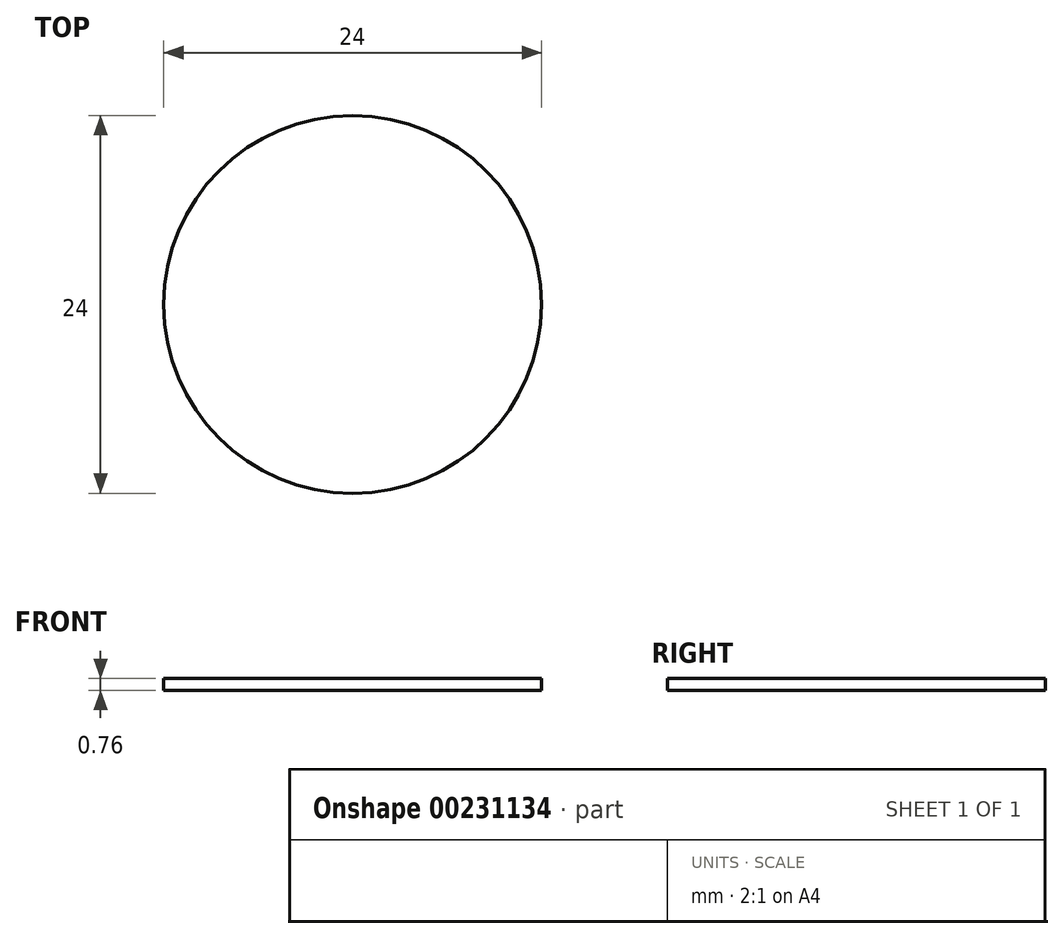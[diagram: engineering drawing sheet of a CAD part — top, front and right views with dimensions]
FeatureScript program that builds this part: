
annotation { "Feature Type Name" : "Feature", "Feature Type Description" : "" }
export const myFeature = defineFeature(function(context is Context, id is Id, definition is map)
    precondition{}
    {
        {
            var Q0;
            Q0=qCreatedBy(makeId("Top.planeOp"),FACE);
            var sketch = newSketch(context, id + "F0", { "sketchPlane" : qUnion([Q0])});
            skCircle(sketch, "E0", {"center": v(0, 0) * mm, "radius": 12 * mm});
            skSolve(sketch);
        }
        {
            var Q0;
            Q0=makeQuery(id+"F0.imprint","IMPRINT",FACE,{"disambiguationData":[TD([[makeQuery(id+"F0.imprint","IMPRINT",EDGE,{"derivedFrom":sQuery(id+"F0.wireOp",EDGE,"E0")}),1.0]])]});
            extrude(context, id + "F1", {"entities" : qUnion([Q0]), "depth" : 0.76 * mm});
        }
    });
